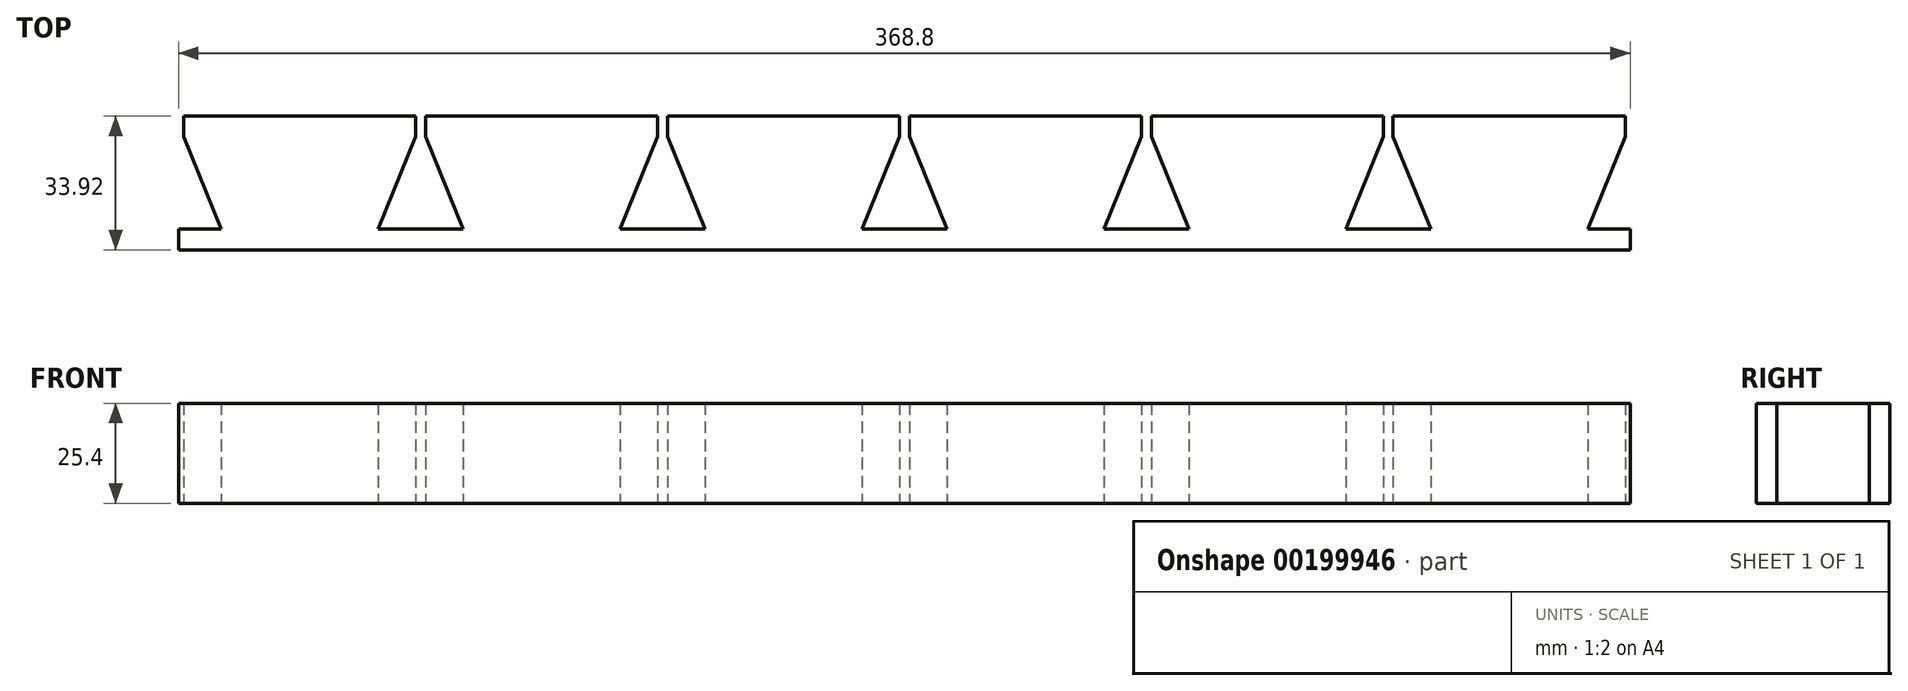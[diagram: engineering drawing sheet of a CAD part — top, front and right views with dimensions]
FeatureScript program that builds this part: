
annotation { "Feature Type Name" : "Feature", "Feature Type Description" : "" }
export const myFeature = defineFeature(function(context is Context, id is Id, definition is map)
    precondition{}
    {
        {
            var Q0;
            Q0=qCreatedBy(makeId("Top.planeOp"),FACE);
            var sketch = newSketch(context, id + "F0", { "sketchPlane" : qUnion([Q0])});
            skLineSegment(sketch, "E0", {"start": v(0, 0) * mm, "end": v(0, 42.6) * mm, "construction": true});
            skLineSegment(sketch, "E1", {"start": v(0, 33.92) * mm, "end": v(29.5, 33.92) * mm});
            skLineSegment(sketch, "E2", {"start": v(29.5, 33.92) * mm, "end": v(29.5, 28.78) * mm});
            skLineSegment(sketch, "E3", {"start": v(29.5, 28.78) * mm, "end": v(19.94, 5.23) * mm});
            skLineSegment(sketch, "E4", {"start": v(29.05, 0) * mm, "end": v(0, 0) * mm});
            skLineSegment(sketch, "E5", {"start": v(19.94, 5.23) * mm, "end": v(30.73, 5.23) * mm});
            skLineSegment(sketch, "E6", {"start": v(30.73, 5.23) * mm, "end": v(30.73, 0) * mm});
            skLineSegment(sketch, "E7", {"start": v(30.73, 0) * mm, "end": v(29.05, 0) * mm});
            skLineSegment(sketch, "E8.MirrorCS", {"start": v(-30.73, 0) * mm, "end": v(-29.05, 0) * mm});
            skLineSegment(sketch, "E9.MirrorCS", {"start": v(-29.05, 0) * mm, "end": v(0, 0) * mm});
            skLineSegment(sketch, "E10.MirrorCS", {"start": v(0, 33.92) * mm, "end": v(-29.5, 33.92) * mm});
            skLineSegment(sketch, "E11.MirrorCS", {"start": v(-29.5, 28.78) * mm, "end": v(-19.94, 5.23) * mm});
            skLineSegment(sketch, "E12.MirrorCS", {"start": v(-30.73, 5.23) * mm, "end": v(-30.73, 0) * mm});
            skLineSegment(sketch, "E13.MirrorCS", {"start": v(-19.94, 5.23) * mm, "end": v(-30.73, 5.23) * mm});
            skLineSegment(sketch, "E14.MirrorCS", {"start": v(-29.5, 33.92) * mm, "end": v(-29.5, 28.78) * mm});
            skLineSegment(sketch, "E15.1.0.0", {"start": v(32.42, 0) * mm, "end": v(61.47, 0) * mm});
            skLineSegment(sketch, "E15.1.0.1", {"start": v(31.98, 28.78) * mm, "end": v(41.53, 5.23) * mm});
            skLineSegment(sketch, "E15.1.0.2", {"start": v(61.47, 33.92) * mm, "end": v(31.98, 33.92) * mm});
            skLineSegment(sketch, "E15.1.0.3", {"start": v(41.53, 5.23) * mm, "end": v(30.73, 5.23) * mm});
            skLineSegment(sketch, "E15.1.0.4", {"start": v(81.41, 5.23) * mm, "end": v(92.2, 5.23) * mm});
            skLineSegment(sketch, "E15.1.0.5", {"start": v(90.51, 0) * mm, "end": v(61.47, 0) * mm});
            skLineSegment(sketch, "E15.1.0.6", {"start": v(61.47, 33.92) * mm, "end": v(90.96, 33.92) * mm});
            skLineSegment(sketch, "E15.1.0.7", {"start": v(61.47, 0) * mm, "end": v(61.47, 42.6) * mm, "construction": true});
            skLineSegment(sketch, "E15.1.0.8", {"start": v(90.96, 28.78) * mm, "end": v(81.41, 5.23) * mm});
            skLineSegment(sketch, "E15.1.0.9", {"start": v(90.96, 33.92) * mm, "end": v(90.96, 28.78) * mm});
            skLineSegment(sketch, "E15.1.0.11", {"start": v(92.2, 0) * mm, "end": v(90.51, 0) * mm});
            skLineSegment(sketch, "E15.1.0.12", {"start": v(30.73, 0) * mm, "end": v(32.42, 0) * mm});
            skLineSegment(sketch, "E15.1.0.13", {"start": v(31.98, 33.92) * mm, "end": v(31.98, 28.78) * mm});
            skLineSegment(sketch, "E15.1.0.14", {"start": v(92.2, 5.23) * mm, "end": v(92.2, 0) * mm});
            skLineSegment(sketch, "E15.2.0.0", {"start": v(93.89, 0) * mm, "end": v(122.94, 0) * mm});
            skLineSegment(sketch, "E15.2.0.1", {"start": v(93.44, 28.78) * mm, "end": v(103, 5.23) * mm});
            skLineSegment(sketch, "E15.2.0.2", {"start": v(122.94, 33.92) * mm, "end": v(93.44, 33.92) * mm});
            skLineSegment(sketch, "E15.2.0.3", {"start": v(103, 5.23) * mm, "end": v(92.2, 5.23) * mm});
            skLineSegment(sketch, "E15.2.0.4", {"start": v(142.88, 5.23) * mm, "end": v(153.67, 5.23) * mm});
            skLineSegment(sketch, "E15.2.0.5", {"start": v(151.98, 0) * mm, "end": v(122.94, 0) * mm});
            skLineSegment(sketch, "E15.2.0.6", {"start": v(122.94, 33.92) * mm, "end": v(152.43, 33.92) * mm});
            skLineSegment(sketch, "E15.2.0.7", {"start": v(122.94, 0) * mm, "end": v(122.94, 42.6) * mm, "construction": true});
            skLineSegment(sketch, "E15.2.0.8", {"start": v(152.43, 28.78) * mm, "end": v(142.88, 5.23) * mm});
            skLineSegment(sketch, "E15.2.0.9", {"start": v(152.43, 33.92) * mm, "end": v(152.43, 28.78) * mm});
            skLineSegment(sketch, "E15.2.0.10", {"start": v(92.2, 5.23) * mm, "end": v(92.2, 0) * mm});
            skLineSegment(sketch, "E15.2.0.11", {"start": v(153.67, 0) * mm, "end": v(151.98, 0) * mm});
            skLineSegment(sketch, "E15.2.0.12", {"start": v(92.2, 0) * mm, "end": v(93.89, 0) * mm});
            skLineSegment(sketch, "E15.2.0.13", {"start": v(93.44, 33.92) * mm, "end": v(93.44, 28.78) * mm});
            skLineSegment(sketch, "E15.2.0.14", {"start": v(153.67, 5.23) * mm, "end": v(153.67, 0) * mm});
            skLineSegment(sketch, "E15.3.0.0", {"start": v(155.36, 0) * mm, "end": v(184.4, 0) * mm});
            skLineSegment(sketch, "E15.3.0.1", {"start": v(154.91, 28.78) * mm, "end": v(164.46, 5.23) * mm});
            skLineSegment(sketch, "E15.3.0.2", {"start": v(184.4, 33.92) * mm, "end": v(154.91, 33.92) * mm});
            skLineSegment(sketch, "E15.3.0.3", {"start": v(164.46, 5.23) * mm, "end": v(153.67, 5.23) * mm});
            skLineSegment(sketch, "E15.3.0.4", {"start": v(204.35, 5.23) * mm, "end": v(215.14, 5.23) * mm});
            skLineSegment(sketch, "E15.3.0.5", {"start": v(213.45, 0) * mm, "end": v(184.4, 0) * mm});
            skLineSegment(sketch, "E15.3.0.6", {"start": v(184.4, 33.92) * mm, "end": v(213.9, 33.92) * mm});
            skLineSegment(sketch, "E15.3.0.7", {"start": v(184.4, 0) * mm, "end": v(184.4, 42.6) * mm, "construction": true});
            skLineSegment(sketch, "E15.3.0.8", {"start": v(213.9, 28.78) * mm, "end": v(204.35, 5.23) * mm});
            skLineSegment(sketch, "E15.3.0.9", {"start": v(213.9, 33.92) * mm, "end": v(213.9, 28.78) * mm});
            skLineSegment(sketch, "E15.3.0.10", {"start": v(153.67, 5.23) * mm, "end": v(153.67, 0) * mm});
            skLineSegment(sketch, "E15.3.0.11", {"start": v(215.14, 0) * mm, "end": v(213.45, 0) * mm});
            skLineSegment(sketch, "E15.3.0.12", {"start": v(153.67, 0) * mm, "end": v(155.36, 0) * mm});
            skLineSegment(sketch, "E15.3.0.13", {"start": v(154.91, 33.92) * mm, "end": v(154.91, 28.78) * mm});
            skLineSegment(sketch, "E15.3.0.14", {"start": v(215.14, 5.23) * mm, "end": v(215.14, 0) * mm});
            skLineSegment(sketch, "E15.4.0.0", {"start": v(216.83, 0) * mm, "end": v(245.87, 0) * mm});
            skLineSegment(sketch, "E15.4.0.1", {"start": v(216.38, 28.78) * mm, "end": v(225.93, 5.23) * mm});
            skLineSegment(sketch, "E15.4.0.2", {"start": v(245.87, 33.92) * mm, "end": v(216.38, 33.92) * mm});
            skLineSegment(sketch, "E15.4.0.3", {"start": v(225.93, 5.23) * mm, "end": v(215.14, 5.23) * mm});
            skLineSegment(sketch, "E15.4.0.4", {"start": v(265.81, 5.23) * mm, "end": v(276.6, 5.23) * mm});
            skLineSegment(sketch, "E15.4.0.5", {"start": v(274.92, 0) * mm, "end": v(245.87, 0) * mm});
            skLineSegment(sketch, "E15.4.0.6", {"start": v(245.87, 33.92) * mm, "end": v(275.36, 33.92) * mm});
            skLineSegment(sketch, "E15.4.0.7", {"start": v(245.87, 0) * mm, "end": v(245.87, 42.6) * mm, "construction": true});
            skLineSegment(sketch, "E15.4.0.8", {"start": v(275.36, 28.78) * mm, "end": v(265.81, 5.23) * mm});
            skLineSegment(sketch, "E15.4.0.9", {"start": v(275.36, 33.92) * mm, "end": v(275.36, 28.78) * mm});
            skLineSegment(sketch, "E15.4.0.10", {"start": v(215.14, 5.23) * mm, "end": v(215.14, 0) * mm});
            skLineSegment(sketch, "E15.4.0.11", {"start": v(276.6, 0) * mm, "end": v(274.92, 0) * mm});
            skLineSegment(sketch, "E15.4.0.12", {"start": v(215.14, 0) * mm, "end": v(216.83, 0) * mm});
            skLineSegment(sketch, "E15.4.0.13", {"start": v(216.38, 33.92) * mm, "end": v(216.38, 28.78) * mm});
            skLineSegment(sketch, "E15.4.0.14", {"start": v(276.6, 5.23) * mm, "end": v(276.6, 0) * mm});
            skLineSegment(sketch, "E15.5.0.0", {"start": v(278.3, 0) * mm, "end": v(307.34, 0) * mm});
            skLineSegment(sketch, "E15.5.0.1", {"start": v(277.85, 28.78) * mm, "end": v(287.4, 5.23) * mm});
            skLineSegment(sketch, "E15.5.0.2", {"start": v(307.34, 33.92) * mm, "end": v(277.85, 33.92) * mm});
            skLineSegment(sketch, "E15.5.0.3", {"start": v(287.4, 5.23) * mm, "end": v(276.6, 5.23) * mm});
            skLineSegment(sketch, "E15.5.0.4", {"start": v(327.28, 5.23) * mm, "end": v(338.07, 5.23) * mm});
            skLineSegment(sketch, "E15.5.0.5", {"start": v(336.39, 0) * mm, "end": v(307.34, 0) * mm});
            skLineSegment(sketch, "E15.5.0.6", {"start": v(307.34, 33.92) * mm, "end": v(336.83, 33.92) * mm});
            skLineSegment(sketch, "E15.5.0.7", {"start": v(307.34, 0) * mm, "end": v(307.34, 42.6) * mm, "construction": true});
            skLineSegment(sketch, "E15.5.0.8", {"start": v(336.83, 28.78) * mm, "end": v(327.28, 5.23) * mm});
            skLineSegment(sketch, "E15.5.0.9", {"start": v(336.83, 33.92) * mm, "end": v(336.83, 28.78) * mm});
            skLineSegment(sketch, "E15.5.0.10", {"start": v(276.6, 5.23) * mm, "end": v(276.6, 0) * mm});
            skLineSegment(sketch, "E15.5.0.11", {"start": v(338.07, 0) * mm, "end": v(336.39, 0) * mm});
            skLineSegment(sketch, "E15.5.0.12", {"start": v(276.6, 0) * mm, "end": v(278.3, 0) * mm});
            skLineSegment(sketch, "E15.5.0.13", {"start": v(277.85, 33.92) * mm, "end": v(277.85, 28.78) * mm});
            skLineSegment(sketch, "E15.5.0.14", {"start": v(338.07, 5.23) * mm, "end": v(338.07, 0) * mm});
            skLineSegment(sketch, "E15.direction1", {"start": v(-30.73, 0) * mm, "end": v(30.73, 0) * mm, "construction": true});
            skSolve(sketch);
        }
        {
            var Q0;
            Q0 = qSketchRegion(id + "F0", true);
            extrude(context, id + "F1", {"entities" : qUnion([Q0]), "depth" : 25.4 * mm});
        }
    });
